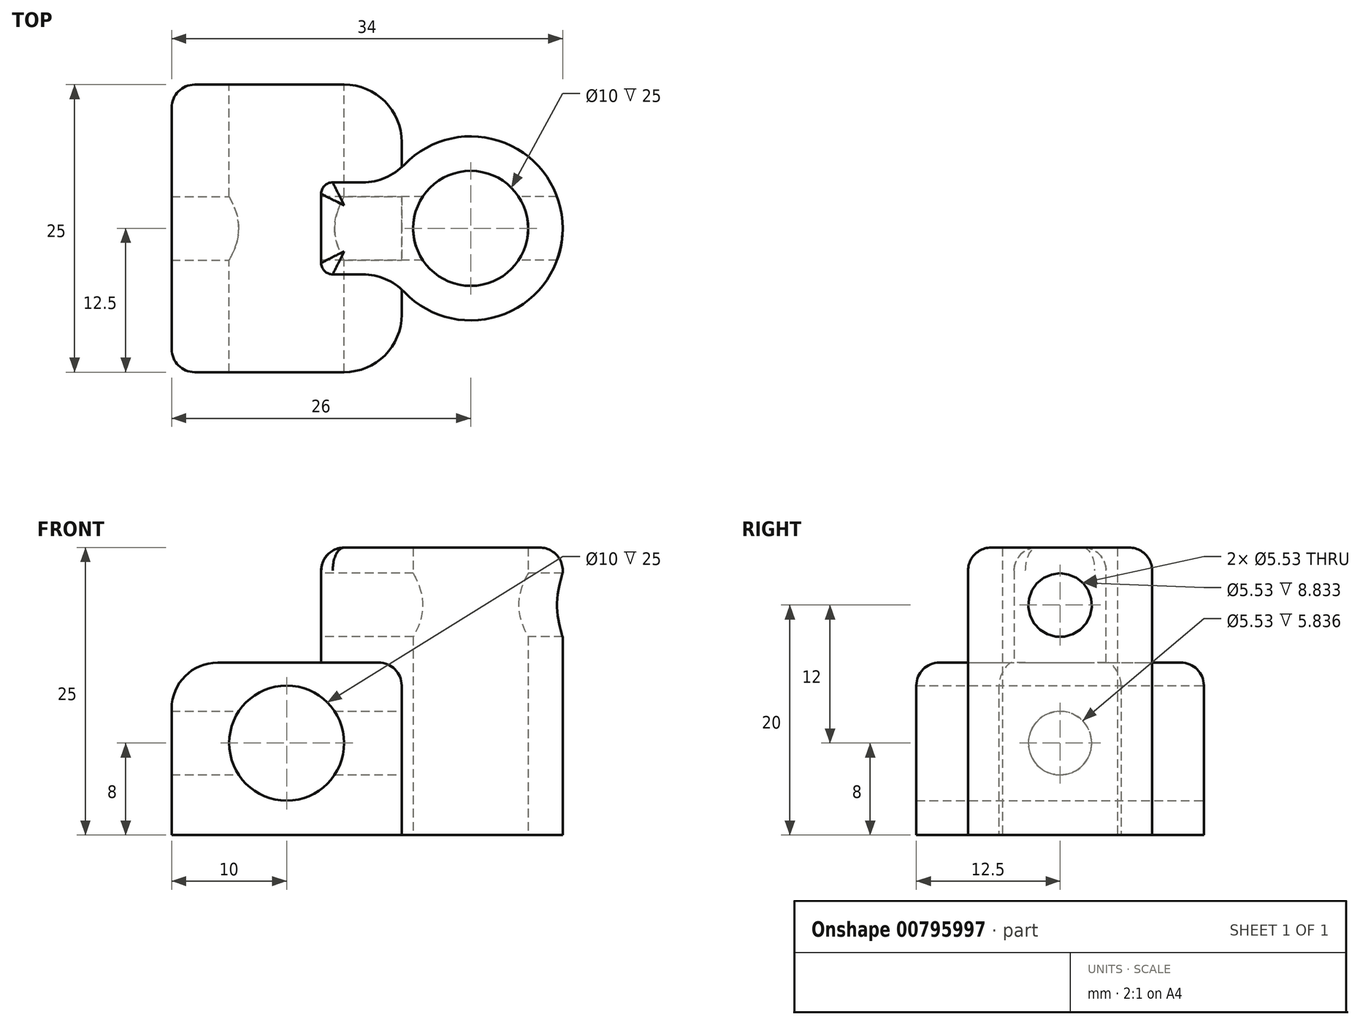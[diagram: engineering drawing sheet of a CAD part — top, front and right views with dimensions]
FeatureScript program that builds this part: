
annotation { "Feature Type Name" : "Feature", "Feature Type Description" : "" }
export const myFeature = defineFeature(function(context is Context, id is Id, definition is map)
    precondition{}
    {
        {
            var Q0;
            Q0=qCreatedBy(makeId("Top.planeOp"),FACE);
            cPlane(context, id + "F0", {"entities" : qUnion([Q0]), "cplaneType" : CPlaneType.OFFSET, "offset" : 25 * mm, "width" : 150 * mm, "height" : 150 * mm});
        }
        {
            var Q0;
            Q0=qCreatedBy(makeId("Top.planeOp"),FACE);
            var sketch = newSketch(context, id + "F1", { "sketchPlane" : qUnion([Q0])});
            skCircle(sketch, "E0", {"center": v(0, 0) * mm, "radius": 8 * mm});
            skCircle(sketch, "E1", {"center": v(0, 0) * mm, "radius": 5 * mm});
            skSolve(sketch);
        }
        {
            var Q0;
            Q0=makeQuery(id+"F1.imprint","IMPRINT",FACE,{"disambiguationData":[TD([[makeQuery(id+"F1.imprint","IMPRINT",EDGE,{"derivedFrom":sQuery(id+"F1.wireOp",EDGE,"E0")}),1.0]])]});
            extrude(context, id + "F2", {"entities" : qUnion([Q0]), "depth" : 25 * mm, "offsetDistance" : 25 * mm});
        }
        {
            var Q0;
            Q0=qCreatedBy(makeId("Front.planeOp"),FACE);
            var sketch = newSketch(context, id + "F3", { "sketchPlane" : qUnion([Q0])});
            skCircle(sketch, "E2", {"center": v(-16, 8) * mm, "radius": 5 * mm});
            skLineSegment(sketch, "E3", {"start": v(-26, 0) * mm, "end": v(-26, 11) * mm});
            skLineSegment(sketch, "E4", {"start": v(-22, 15) * mm, "end": v(-6, 15) * mm});
            skLineSegment(sketch, "E5", {"start": v(-6, 15) * mm, "end": v(-6, 0) * mm});
            skLineSegment(sketch, "E6", {"start": v(-6, 0) * mm, "end": v(-26, 0) * mm});
            skArc(sketch, "E7", {"start": v(-26, 11) * mm, "mid": v(-24.83, 13.83) * mm, "end": v(-22, 15) * mm});
            skSolve(sketch);
        }
        {
            var Q0;
            Q0 = qSketchRegion(id + "F3", true);
            extrude(context, id + "F4", {"entities" : qUnion([Q0]), "operationType" : NewBodyOperationType.ADD, "endBound" : BoundingType.SYMMETRIC, "depth" : 25 * mm, "offsetDistance" : 25 * mm});
        }
        {
            var Q0;
            Q0=qCreatedBy(makeId("Front.planeOp"),FACE);
            var sketch = newSketch(context, id + "F5", { "sketchPlane" : qUnion([Q0])});
            skLineSegment(sketch, "E8.0", {"start": v(-13, 15) * mm, "end": v(-8, 15) * mm});
            skLineSegment(sketch, "E9", {"start": v(-13, 15) * mm, "end": v(-13, 25) * mm});
            skLineSegment(sketch, "E10", {"start": v(-13, 25) * mm, "end": v(-5.84, 25) * mm});
            skPoint(sketch, "E11.orphan", {"position": v(-22, 15) * mm});
            skPoint(sketch, "E12.orphan", {"position": v(-6, 15) * mm});
            skLineSegment(sketch, "E13", {"start": v(-5.84, 25) * mm, "end": v(-5.84, 14.96) * mm});
            skPoint(sketch, "E13.startSnap0", {"position": v(-10.5, 25) * mm});
            skPoint(sketch, "E14.orphan", {"position": v(-8, 25) * mm});
            skLineSegment(sketch, "E15", {"start": v(-8, 15) * mm, "end": v(-5.84, 14.96) * mm});
            skSolve(sketch);
        }
        {
            var Q0;
            Q0 = qSketchRegion(id + "F5", true);
            extrude(context, id + "F6", {"entities" : qUnion([Q0]), "operationType" : NewBodyOperationType.ADD, "endBound" : BoundingType.SYMMETRIC, "depth" : 8 * mm, "offsetDistance" : 25 * mm});
        }
        {
            var Q0;
            Q0=makeQuery(id+"F6.opExtrude","SWEPT_FACE",FACE,{"disambiguationData":[OSD([sQuery(id+"F5.wireOp",EDGE,"E9")])]});
            var sketch = newSketch(context, id + "F7", { "sketchPlane" : qUnion([Q0])});
            skCircle(sketch, "E16", {"center": v(0, 20) * mm, "radius": 2.76 * mm});
            skSolve(sketch);
        }
        {
            var Q0;
            Q0 = qSketchRegion(id + "F7", true);
            extrude(context, id + "F8", {"entities" : qUnion([Q0]), "operationType" : NewBodyOperationType.REMOVE, "oppositeDirection" : true, "depth" : 25 * mm, "offsetDistance" : 25 * mm});
        }
        {
            var Q0;
            {var subQ0=sQuery(id+"F3.wireOp",EDGE,"E4");var subQ2=sQuery(id+"F3.wireOp",EDGE,"E6");var subQ3=sQuery(id+"F3.wireOp",EDGE,"E5");Q0=makeQuery(id+"F4.boolean.opBoolean","SPLIT",FACE,{"disambiguationData":[TD([makeQuery(id+"F4.opExtrude","CAP_FACE",FACE,{"disambiguationData":[OSD([sQuery(id+"F3.wireOp",EDGE,"E2"),sQuery(id+"F3.wireOp",EDGE,"E3"),subQ0,subQ3,subQ2,sQuery(id+"F3.wireOp",EDGE,"E7")])],"isStart":false})])],"derivedFrom":makeQuery(id+"F4.opExtrude","SWEPT_FACE",FACE,{"disambiguationData":[OSD([subQ3])]})});}
            var sketch = newSketch(context, id + "F9", { "sketchPlane" : qUnion([Q0])});
            skCircle(sketch, "E17", {"center": v(0, 8) * mm, "radius": 2.76 * mm});
            skSolve(sketch);
        }
        {
            var Q0;
            Q0 = qSketchRegion(id + "F9", true);
            extrude(context, id + "F10", {"entities" : qUnion([Q0]), "operationType" : NewBodyOperationType.REMOVE, "oppositeDirection" : true, "depth" : 50 * mm, "offsetDistance" : 25 * mm});
        }
        {
            var Q0;
            Q0=makeQuery(id+"F6.boolean.opBoolean","INTERSECT",EDGE,{"derivedFrom":[makeQuery(id+"F2.opExtrude","SWEPT_FACE",FACE,{"disambiguationData":[OSD([sQuery(id+"F1.wireOp",EDGE,"E0")])]}),makeQuery(id+"F6.opExtrude","CAP_FACE",FACE,{"disambiguationData":[OSD([sQuery(id+"F5.wireOp",EDGE,"E8.0"),sQuery(id+"F5.wireOp",EDGE,"E9"),sQuery(id+"F5.wireOp",EDGE,"E10"),sQuery(id+"F5.wireOp",EDGE,"E13"),sQuery(id+"F5.wireOp",EDGE,"E15")])],"isStart":false})]});
            var Q1;
            Q1=makeQuery(id+"F6.boolean.opBoolean","INTERSECT",EDGE,{"derivedFrom":[makeQuery(id+"F2.opExtrude","SWEPT_FACE",FACE,{"disambiguationData":[OSD([sQuery(id+"F1.wireOp",EDGE,"E0")])]}),makeQuery(id+"F6.opExtrude","CAP_FACE",FACE,{"disambiguationData":[OSD([sQuery(id+"F5.wireOp",EDGE,"E8.0"),sQuery(id+"F5.wireOp",EDGE,"E9"),sQuery(id+"F5.wireOp",EDGE,"E10"),sQuery(id+"F5.wireOp",EDGE,"E13"),sQuery(id+"F5.wireOp",EDGE,"E15")])],"isStart":true})]});
            var Q2;
            Q2=makeQuery(id+"F4.opExtrude","CAP_EDGE",EDGE,{"disambiguationData":[OSD([sQuery(id+"F3.wireOp",EDGE,"E5")])],"isStart":false});
            var Q3;
            Q3=makeQuery(id+"F4.opExtrude","CAP_EDGE",EDGE,{"disambiguationData":[OSD([sQuery(id+"F3.wireOp",EDGE,"E5")])],"isStart":true});
            fillet(context, id + "F11", {"entities" : qUnion([Q0, Q1, Q2, Q3]), "radius" : 5 * mm, "tangentPropagation" : true, "allowEdgeOverflow" : false});
        }
        {
            var Q0;
            Q0=makeQuery(id+"F6.opExtrude","CAP_EDGE",EDGE,{"disambiguationData":[OSD([sQuery(id+"F5.wireOp",EDGE,"E9")])],"isStart":true});
            var Q1;
            Q1=makeQuery(id+"F6.opExtrude","CAP_EDGE",EDGE,{"disambiguationData":[OSD([sQuery(id+"F5.wireOp",EDGE,"E9")])],"isStart":false});
            fillet(context, id + "F12", {"entities" : qUnion([Q0, Q1]), "radius" : 1 * mm, "tangentPropagation" : true, "allowEdgeOverflow" : false});
        }
        {
            var Q0;
            Q0=makeQuery(id+"F2.opExtrude","CAP_EDGE",EDGE,{"disambiguationData":[OSD([sQuery(id+"F1.wireOp",EDGE,"E0")])],"isStart":false});
            fillet(context, id + "F13", {"entities" : qUnion([Q0]), "radius" : 2 * mm, "tangentPropagation" : true, "allowEdgeOverflow" : false});
        }
        {
            var Q0;
            Q0=makeQuery(id+"F4.opExtrude","CAP_EDGE",EDGE,{"disambiguationData":[OSD([sQuery(id+"F3.wireOp",EDGE,"E3")])],"isStart":false});
            var Q1;
            Q1=makeQuery(id+"F4.opExtrude","CAP_EDGE",EDGE,{"disambiguationData":[OSD([sQuery(id+"F3.wireOp",EDGE,"E3")])],"isStart":true});
            fillet(context, id + "F14", {"entities" : qUnion([Q0, Q1]), "radius" : 2 * mm, "tangentPropagation" : true, "allowEdgeOverflow" : false});
        }
    });
